# Revit family: PRD_FrankeWS_WlHngWshBsns_AnimaWashbasin_BS204,204-M,205,205-M
name_source: partatom
category: Plumbing Fixtures
revit_build: Autodesk Revit 2018 (Build: 20190510_1515(x64)
units: mm (PartAtom-declared; Revit-internal decimal feet)

## family parameters
Cut with Voids When Loaded = No
Host = Face
OmniClass Number = 23.45.05.14.14
OmniClass Title = Sinks/Lavatories
Part Type = Normal
Room Calculation Point = No
Round Connector Dimension = Use Diameter
Shared = No

## types (4) — shared parameters
AssetType = Fixed
Category = Pr_40_20_96_96, Wall-hung wash basins
Color = Stainless steel
Default Elevation = 850 mm  [stored 2.78871 ft]
DrainSize = DN 32 (1 1/4 inch.)
DurationUnit = year
Features = stainless steel, 1.00 mm, satin finished, wall mounting, 550x155x450 mm (WxHxD)
Finish = Satin finished
Form = Wall hung wash basin
IfcExportAs = IfcSanitaryTerminalType
IfcExportType = WASHHANDBASIN
IntegralAccessories = Incl. stainless steel screws and dowels
Manufacturer = KWC Group AG
ManufacturerName = KWC Group AG
ManufacturerURL = www.kwc.com
Material = Stainless steel
MaterialsBody = Stainless steel 1.4301
MaterialsFinishAndColour = Stainless steel, satin finished
NBSDescription = Wall hung wash basins
NBSReference = 45-35-70/369
NominalDepth = 450 mm  [stored 1.47638 ft]
NominalHeight = 155 mm  [stored 0.50853 ft]
NominalWidth = 550 mm
ProductInformation = https://pim.kwc.com
Shape = Oval
Size = 550 x 450 x 155 mm
TrapCoverMaterial = PRD_AR_StainlessSteel_SatinFinished
URL = www.kwc.com
Uniclass2015Code = Pr_40_20_96_96
Uniclass2015Title = Wall-hung wash basins
Uniclass2015Version = Products v1.10
Version = 1
WarrantyDurationUnit = year
WashHandBasinMounting = WallHung
WashHandBasinType = HandRinse
WashbasinMaterial = PRD_AR_StainlessSteel_SatinFinished
WasteSize = 32  [stored 0.104987 ft]
WaterSupplyOverflowAndWasteHolesOverflow = None
WaterSupplyOverflowAndWasteHolesWaste = Center-Back

## per-type parameters (varying)
| type | BIMObjectName | Description | GrossWeight | Model | ModelNumber | ModelReference | Name | NetWeight | Taphole | Type | WaterSupplyOverflowAndWasteHolesWaterSupply |
| BS204 - without taphole | PRD_AR_WallHungWashBasins_AnimaWashbasin_BS204 | Single wash basin for wall mounting, stainless steel, surface satin finished, material thickness 1 mm, seamless welded bowl with diameter 500x335x155 mm, oval shape, 90 mm tap ledge, prewelded mounting brackets, with soap dish, incl. screws and dowels. without overflow, 1 1/4 flat perforated waste | 4.64 kg | BS204 | 2000090016 | BS204 | ANIMA wall-hung wash basin BS204 | 3.68 kg | No | BS204 | No tapholes |
| BS204-M - with taphole | PRD_AR_WallHungWashBasins_AnimaWashbasin_BS204-M | Single wash basin for wall mounting, stainless steel, surface satin finished, material thickness 1 mm, seamless welded bowl with diameter 500x335x155 mm, oval shape, 90 mm tap ledge, prewelded mounting brackets, with soap dish, incl. screws and dowels. without overflow, 1 1/4 flat perforated waste, with tap hole | 4.32 kg | BS204-M | 2000103078 | BS204-M | ANIMA wall-hung wash basin BS204-M | 4.22 kg | Yes | BS204 | Single tap hole, middle, 35 mm |
| BS205 - without taphole | PRD_AR_WallHungWashBasins_AnimaWashbasin_BS205 | Single wash basin for wall mounting, stainless steel, surface satin finished, material thickness 1 mm, seamless welded bowl with diameter 500x335x155 mm, oval shape, 90 mm tap ledge, prewelded mounting brackets, with soap dish, incl. screws and dowels. with overflow, 1 1/4 plug waste | 4.80 kg | BS205 | 2000090017 | BS205 | ANIMA wall-hung wash basin BS205 | 3.63 kg | No | BS205 | No tapholes |
| BS205-M - with taphole | PRD_AR_WallHungWashBasins_AnimaWashbasin_BS205-M | Single wash basin for wall mounting, stainless steel, surface satin finished, material thickness 1 mm, seamless welded bowl with diameter 500x335x155 mm, oval shape, 90 mm tap ledge, prewelded mounting brackets, with soap dish, incl. screws and dowels. plug valve with 1 1/4 with overflow and tap hole | 3.73 kg | BS205-M | 2000103080 | BS205-M | ANIMA wall-hung wash basin BS205-M | 3.63 kg | Yes | BS205 | Single tap hole, middle, 35 mm |

note: [stored X ft] marks values corroborated as IEEE doubles in the binary element streams (Revit-internal decimal feet)

## geometry (parser evidence)
native form markers: Sweep x9
no freeform markers — native parametric forms only
